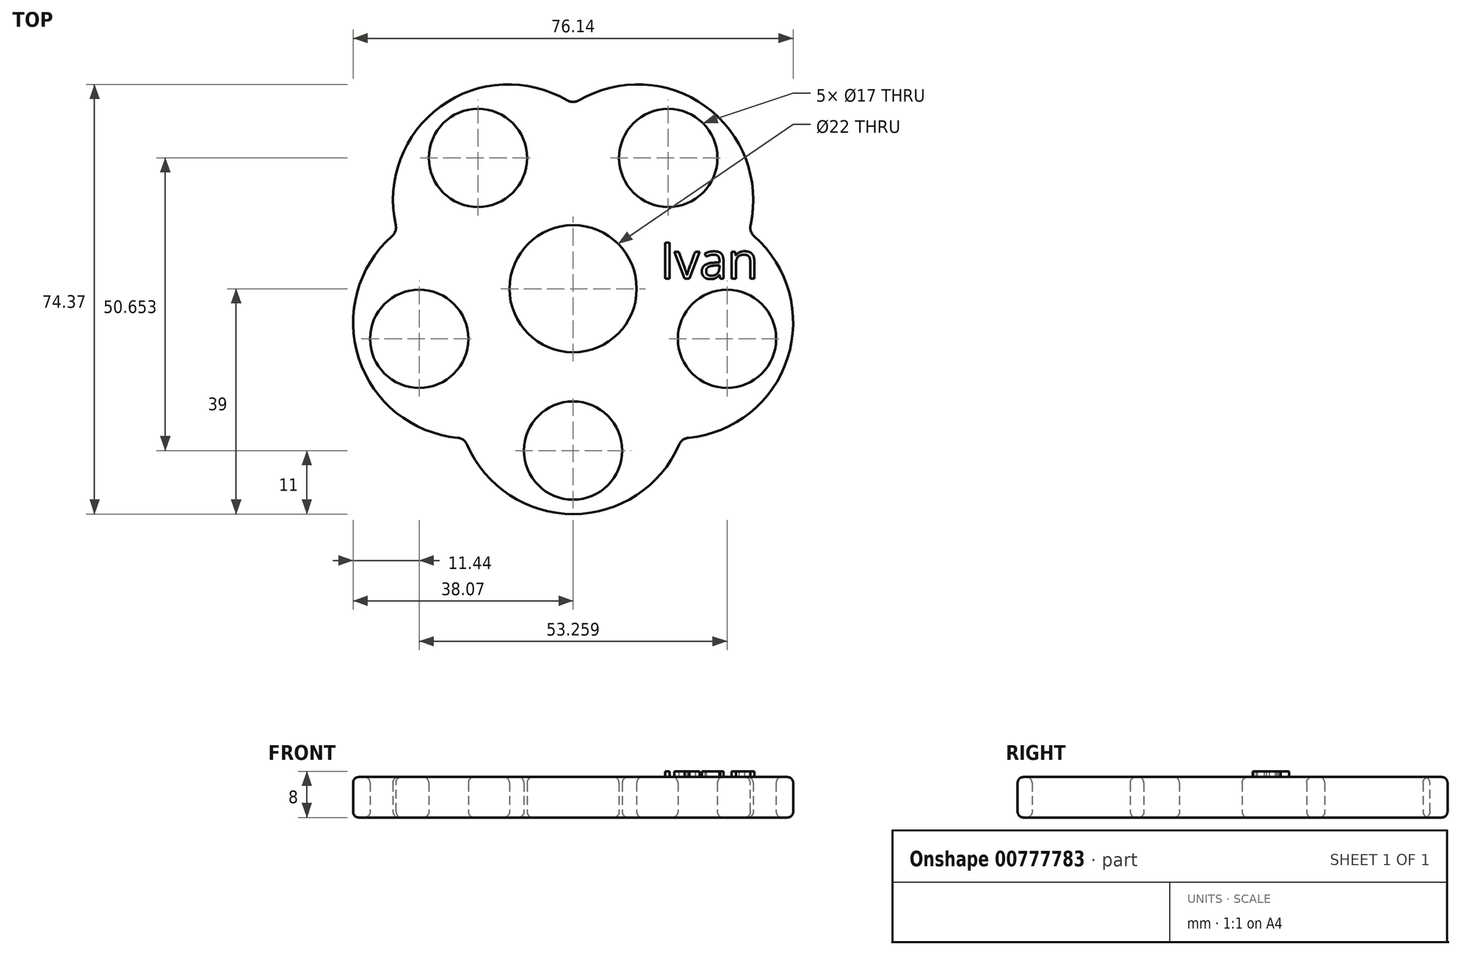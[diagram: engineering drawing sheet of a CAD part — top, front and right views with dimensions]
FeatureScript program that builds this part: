
annotation { "Feature Type Name" : "Feature", "Feature Type Description" : "" }
export const myFeature = defineFeature(function(context is Context, id is Id, definition is map)
    precondition{}
    {
        {
            var Q0;
            Q0=qCreatedBy(makeId("Top.planeOp"),FACE);
            var sketch = newSketch(context, id + "F0", { "sketchPlane" : qUnion([Q0])});
            skCircle(sketch, "E0.cCircle", {"center": v(0, 0) * mm, "radius": 19 * mm, "construction": true});
            skPoint(sketch, "E0.0.midPoint", {"position": v(11.17, 15.37) * mm});
            skArc(sketch, "E1", {"start": v(0, 31.96) * mm, "mid": v(-22.92, 31.55) * mm, "end": v(-30.4, 9.88) * mm});
            skArc(sketch, "E2", {"start": v(30.4, 9.88) * mm, "mid": v(22.92, 31.55) * mm, "end": v(0, 31.96) * mm});
            skArc(sketch, "E3", {"start": v(18.79, -25.86) * mm, "mid": v(37.1, -12.05) * mm, "end": v(30.4, 9.88) * mm});
            skArc(sketch, "E4", {"start": v(-18.79, -25.86) * mm, "mid": v(0, -39) * mm, "end": v(18.79, -25.86) * mm});
            skArc(sketch, "E5", {"start": v(-30.4, 9.88) * mm, "mid": v(-37.1, -12.05) * mm, "end": v(-18.79, -25.86) * mm});
            skCircle(sketch, "E6", {"center": v(0, 0) * mm, "radius": 31.96 * mm, "construction": true});
            skCircle(sketch, "E7", {"center": v(0, 0) * mm, "radius": 11 * mm});
            skCircle(sketch, "E8", {"center": v(-16.46, 22.65) * mm, "radius": 8.5 * mm});
            skCircle(sketch, "E9", {"center": v(16.46, 22.65) * mm, "radius": 8.5 * mm});
            skCircle(sketch, "E10", {"center": v(26.63, -8.65) * mm, "radius": 8.5 * mm});
            skCircle(sketch, "E11", {"center": v(0, -28) * mm, "radius": 8.5 * mm});
            skCircle(sketch, "E12", {"center": v(-26.63, -8.65) * mm, "radius": 8.5 * mm});
            skCircle(sketch, "E13", {"center": v(0, 0) * mm, "radius": 28 * mm, "construction": true});
            skLineSegment(sketch, "E14", {"start": v(0, 0) * mm, "end": v(0, 61.86) * mm, "construction": true});
            skLineSegment(sketch, "E15", {"start": v(0, 0) * mm, "end": v(34.94, 48.1) * mm, "construction": true});
            skLineSegment(sketch, "E16", {"start": v(0, 0) * mm, "end": v(70.3, -22.84) * mm, "construction": true});
            skLineSegment(sketch, "E17", {"start": v(0, 0) * mm, "end": v(0, -36.5) * mm, "construction": true});
            skLineSegment(sketch, "E18", {"start": v(0, 0) * mm, "end": v(-61.86, -20.1) * mm, "construction": true});
            skLineSegment(sketch, "E19", {"start": v(0, 0) * mm, "end": v(-31.6, 43.5) * mm, "construction": true});
            skSolve(sketch);
        }
        {
            var Q0;
            Q0=qSketchRegion(id+"F0",true);
            extrude(context, id + "F1", {"entities" : qUnion([Q0]), "depth" : 7 * mm, "offsetDistance" : 25.4 * mm});
        }
        {
            var Q0;
            Q0=makeQuery(id+"F1.opExtrude","SWEPT_EDGE",EDGE,{"disambiguationData":[OSD([sQuery(id+"F0.wireOp",EDGE,"E3"),sQuery(id+"F0.wireOp",EDGE,"E4")])]});
            var Q1;
            Q1=makeQuery(id+"F1.opExtrude","SWEPT_EDGE",EDGE,{"disambiguationData":[OSD([sQuery(id+"F0.wireOp",EDGE,"E2"),sQuery(id+"F0.wireOp",EDGE,"E3")])]});
            var Q2;
            Q2=makeQuery(id+"F1.opExtrude","SWEPT_EDGE",EDGE,{"disambiguationData":[OSD([sQuery(id+"F0.wireOp",EDGE,"E1"),sQuery(id+"F0.wireOp",EDGE,"E2")])]});
            var Q3;
            Q3=makeQuery(id+"F1.opExtrude","SWEPT_EDGE",EDGE,{"disambiguationData":[OSD([sQuery(id+"F0.wireOp",EDGE,"E1"),sQuery(id+"F0.wireOp",EDGE,"E5")])]});
            var Q4;
            Q4=makeQuery(id+"F1.opExtrude","SWEPT_EDGE",EDGE,{"disambiguationData":[OSD([sQuery(id+"F0.wireOp",EDGE,"E4"),sQuery(id+"F0.wireOp",EDGE,"E5")])]});
            fillet(context, id + "F2", {"entities" : qUnion([Q0, Q1, Q2, Q3, Q4]), "radius" : 2 * mm, "tangentPropagation" : true, "allowEdgeOverflow" : false});
        }
        {
            var Q0;
            Q0=makeQuery(id+"F1.opExtrude","CAP_FACE",FACE,{"disambiguationData":[OSD([sQuery(id+"F0.wireOp",EDGE,"E1"),sQuery(id+"F0.wireOp",EDGE,"E2"),sQuery(id+"F0.wireOp",EDGE,"E3"),sQuery(id+"F0.wireOp",EDGE,"E4"),sQuery(id+"F0.wireOp",EDGE,"E5"),sQuery(id+"F0.wireOp",EDGE,"E7"),sQuery(id+"F0.wireOp",EDGE,"E8"),sQuery(id+"F0.wireOp",EDGE,"E9"),sQuery(id+"F0.wireOp",EDGE,"E10"),sQuery(id+"F0.wireOp",EDGE,"E11"),sQuery(id+"F0.wireOp",EDGE,"E12")])],"isStart":false});
            var Q1;
            Q1=makeQuery(id+"F1.opExtrude","CAP_FACE",FACE,{"disambiguationData":[OSD([sQuery(id+"F0.wireOp",EDGE,"E1"),sQuery(id+"F0.wireOp",EDGE,"E2"),sQuery(id+"F0.wireOp",EDGE,"E3"),sQuery(id+"F0.wireOp",EDGE,"E4"),sQuery(id+"F0.wireOp",EDGE,"E5"),sQuery(id+"F0.wireOp",EDGE,"E7"),sQuery(id+"F0.wireOp",EDGE,"E8"),sQuery(id+"F0.wireOp",EDGE,"E9"),sQuery(id+"F0.wireOp",EDGE,"E10"),sQuery(id+"F0.wireOp",EDGE,"E11"),sQuery(id+"F0.wireOp",EDGE,"E12")])],"isStart":true});
            fillet(context, id + "F3", {"entities" : qUnion([Q0, Q1]), "radius" : 1 * mm, "tangentPropagation" : true, "allowEdgeOverflow" : false});
        }
        {
            var Q0;
            Q0=makeQuery(id+"F1.opExtrude","CAP_FACE",FACE,{"disambiguationData":[OSD([sQuery(id+"F0.wireOp",EDGE,"E1"),sQuery(id+"F0.wireOp",EDGE,"E2"),sQuery(id+"F0.wireOp",EDGE,"E3"),sQuery(id+"F0.wireOp",EDGE,"E4"),sQuery(id+"F0.wireOp",EDGE,"E5"),sQuery(id+"F0.wireOp",EDGE,"E7"),sQuery(id+"F0.wireOp",EDGE,"E8"),sQuery(id+"F0.wireOp",EDGE,"E9"),sQuery(id+"F0.wireOp",EDGE,"E10"),sQuery(id+"F0.wireOp",EDGE,"E11"),sQuery(id+"F0.wireOp",EDGE,"E12")])],"isStart":false});
            var sketch = newSketch(context, id + "F4", { "sketchPlane" : qUnion([Q0])});
            skText(sketch, "E20", { "text": "Ivan", "fontName": "OpenSans-Regular.ttf"});
            const initialGuessF4  = {"E20": [0.01509, 0.00176, 1, 0, 0.00626]};
            skSetInitialGuess(sketch, initialGuessF4);
            skSolve(sketch);
        }
        {
            var Q0;
            Q0=qSketchRegion(id+"F4",true);
            extrude(context, id + "F5", {"entities" : qUnion([Q0]), "operationType" : NewBodyOperationType.ADD, "depth" : 1 * mm, "offsetDistance" : 25 * mm});
        }
    });
